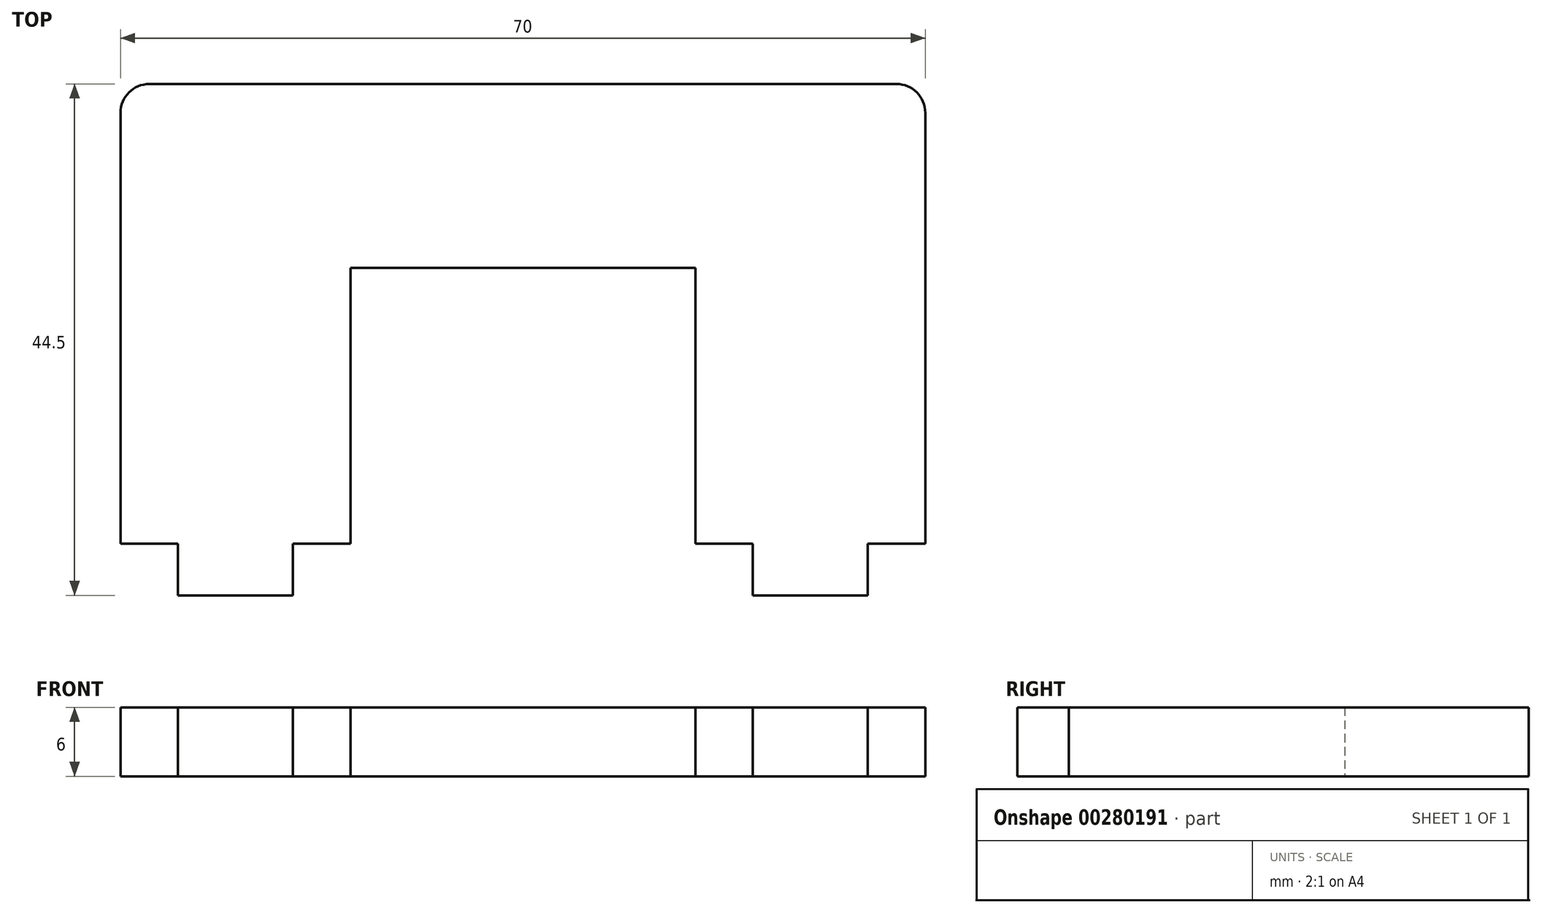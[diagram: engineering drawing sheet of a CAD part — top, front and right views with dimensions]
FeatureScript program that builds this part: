
annotation { "Feature Type Name" : "Feature", "Feature Type Description" : "" }
export const myFeature = defineFeature(function(context is Context, id is Id, definition is map)
    precondition{}
    {
        {
            var Q0;
            Q0=qCreatedBy(makeId("Top.planeOp"),FACE);
            var sketch = newSketch(context, id + "F0", { "sketchPlane" : qUnion([Q0])});
            skLineSegment(sketch, "E0", {"start": v(-32.5, 16) * mm, "end": v(32.5, 16) * mm});
            skLineSegment(sketch, "E1", {"start": v(35, 13.5) * mm, "end": v(35, -24) * mm});
            skLineSegment(sketch, "E2", {"start": v(35, -24) * mm, "end": v(30, -24) * mm});
            skLineSegment(sketch, "E3", {"start": v(30, -24) * mm, "end": v(30, -28.5) * mm});
            skLineSegment(sketch, "E4", {"start": v(30, -28.5) * mm, "end": v(20, -28.5) * mm});
            skLineSegment(sketch, "E5", {"start": v(20, -28.5) * mm, "end": v(20, -24) * mm});
            skLineSegment(sketch, "E6", {"start": v(20, -24) * mm, "end": v(15, -24) * mm});
            skLineSegment(sketch, "E7", {"start": v(15, -24) * mm, "end": v(15, 0) * mm});
            skLineSegment(sketch, "E8", {"start": v(15, 0) * mm, "end": v(-15, 0) * mm});
            skLineSegment(sketch, "E9", {"start": v(-15, 0) * mm, "end": v(-15, -24) * mm});
            skLineSegment(sketch, "E10", {"start": v(-15, -24) * mm, "end": v(-20, -24) * mm});
            skLineSegment(sketch, "E11", {"start": v(-20, -24) * mm, "end": v(-20, -28.5) * mm});
            skLineSegment(sketch, "E12", {"start": v(-20, -28.5) * mm, "end": v(-30, -28.5) * mm});
            skLineSegment(sketch, "E13", {"start": v(-30, -28.5) * mm, "end": v(-30, -24) * mm});
            skLineSegment(sketch, "E14", {"start": v(-30, -24) * mm, "end": v(-35, -24) * mm});
            skLineSegment(sketch, "E15", {"start": v(-35, -24) * mm, "end": v(-35, 13.5) * mm});
            skPoint(sketch, "E16", {"position": v(0, 0) * mm});
            skPoint(sketch, "E17", {"position": v(-25, -28.5) * mm});
            skPoint(sketch, "E18", {"position": v(25, -28.5) * mm});
            skPoint(sketch, "E19.visualSharp", {"position": v(-35, 16) * mm});
            skArc(sketch, "E19.filletArc", {"start": v(-32.5, 16) * mm, "mid": v(-34.27, 15.27) * mm, "end": v(-35, 13.5) * mm});
            skPoint(sketch, "E20.visualSharp", {"position": v(35, 16) * mm});
            skArc(sketch, "E20.filletArc", {"start": v(35, 13.5) * mm, "mid": v(34.27, 15.27) * mm, "end": v(32.5, 16) * mm});
            skSolve(sketch);
        }
        {
            var Q0;
            Q0 = qSketchRegion(id + "F0", true);
            extrude(context, id + "F1", {"entities" : qUnion([Q0]), "depth" : 6 * mm});
        }
    });
